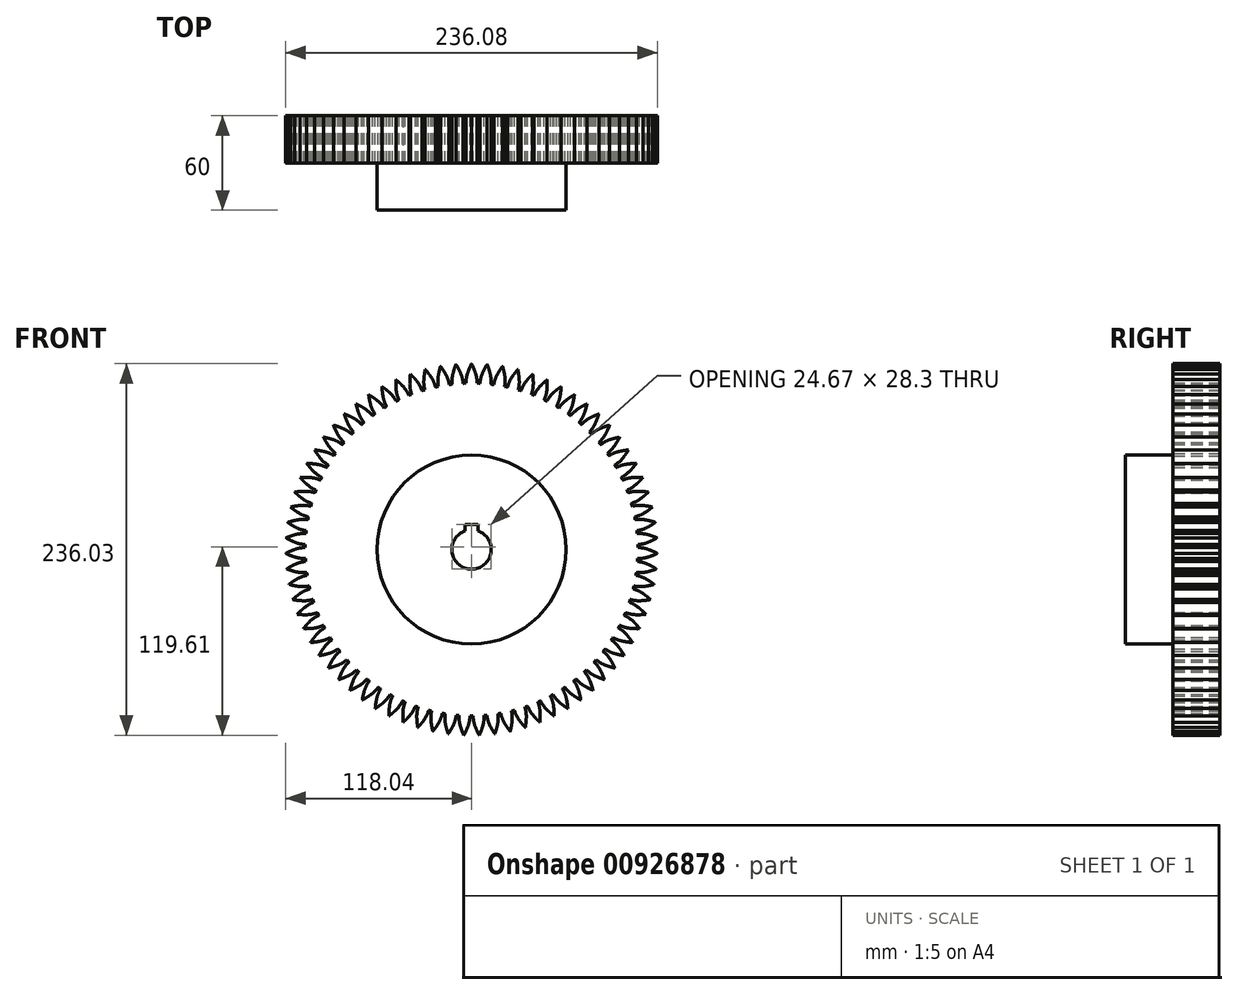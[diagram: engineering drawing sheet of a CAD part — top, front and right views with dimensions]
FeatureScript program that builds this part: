
annotation { "Feature Type Name" : "Feature", "Feature Type Description" : "" }
export const myFeature = defineFeature(function(context is Context, id is Id, definition is map)
    precondition{}
    {
        {
            var Q0;
            Q0=qCreatedBy(makeId("Front.planeOp"),FACE);
            var sketch = newSketch(context, id + "F0", { "sketchPlane" : qUnion([Q0])});
            skCircle(sketch, "E0", {"center": v(0, 0) * mm, "radius": 105.72 * mm});
            skSolve(sketch);
        }
        {
            var Q0;
            Q0=qSketchRegion(id+"F0",true);
            extrude(context, id + "F1", {"entities" : qUnion([Q0]), "depth" : 30 * mm, "offsetDistance" : 25 * mm});
        }
        {
            var Q0;
            Q0=qCreatedBy(makeId("Front.planeOp"),FACE);
            var sketch = newSketch(context, id + "F2", { "sketchPlane" : qUnion([Q0])});
            skCircle(sketch, "E1", {"center": v(0, 0) * mm, "radius": 112.5 * mm, "construction": true});
            skArc(sketch, "E2", {"start": v(50.93, 92.64) * mm, "mid": v(32.1, 100.72) * mm, "end": v(12.06, 105.02) * mm, "construction": true});
            skLineSegment(sketch, "E3", {"start": v(-2.36, 112.48) * mm, "end": v(2.36, 112.48) * mm, "construction": true});
            skLineSegment(sketch, "E4", {"start": v(0, 0) * mm, "end": v(-2.36, 112.48) * mm, "construction": true});
            skLineSegment(sketch, "E5", {"start": v(-2.36, 112.48) * mm, "end": v(34.07, 100.08) * mm, "construction": true});
            skLineSegment(sketch, "E6", {"start": v(0, 0) * mm, "end": v(34.07, 100.08) * mm, "construction": true});
            skLineSegment(sketch, "E7.1.0", {"start": v(0, 0) * mm, "end": v(37.54, 98.83) * mm, "construction": true});
            skLineSegment(sketch, "E7.1.1", {"start": v(1.57, 112.49) * mm, "end": v(37.54, 98.83) * mm, "construction": true});
            skLineSegment(sketch, "E7.2.0", {"start": v(0, 0) * mm, "end": v(40.97, 97.46) * mm, "construction": true});
            skLineSegment(sketch, "E7.2.1", {"start": v(5.5, 112.37) * mm, "end": v(40.97, 97.46) * mm, "construction": true});
            skLineSegment(sketch, "E7.3.0", {"start": v(0, 0) * mm, "end": v(44.34, 95.97) * mm, "construction": true});
            skLineSegment(sketch, "E7.3.1", {"start": v(9.41, 112.1) * mm, "end": v(44.34, 95.97) * mm, "construction": true});
            skLineSegment(sketch, "E7.4.0", {"start": v(0, 0) * mm, "end": v(47.66, 94.36) * mm, "construction": true});
            skLineSegment(sketch, "E7.4.1", {"start": v(13.32, 111.7) * mm, "end": v(47.66, 94.36) * mm, "construction": true});
            skLineSegment(sketch, "E7.5.0", {"start": v(0, 0) * mm, "end": v(50.93, 92.64) * mm, "construction": true});
            skLineSegment(sketch, "E7.5.1", {"start": v(17.21, 111.18) * mm, "end": v(50.93, 92.64) * mm, "construction": true});
            skLineSegment(sketch, "E7.anchor2", {"start": v(0, 0) * mm, "end": v(17.21, 111.18) * mm, "construction": true});
            skLineSegment(sketch, "E8", {"start": v(1.57, 112.49) * mm, "end": v(-1.88, 113.8) * mm, "construction": true});
            skLineSegment(sketch, "E9", {"start": v(5.5, 112.37) * mm, "end": v(-1.3, 115.23) * mm, "construction": true});
            skLineSegment(sketch, "E10", {"start": v(9.41, 112.1) * mm, "end": v(-0.64, 116.75) * mm, "construction": true});
            skLineSegment(sketch, "E11", {"start": v(13.32, 111.7) * mm, "end": v(0.15, 118.36) * mm, "construction": true});
            skLineSegment(sketch, "E12", {"start": v(17.21, 111.18) * mm, "end": v(1.04, 120.06) * mm, "construction": true});
            skFitSpline(sketch, "E13", {"points": [v(-2.36, 112.48) * mm, v(-1.88, 113.8) * mm, v(-1.3, 115.23) * mm, v(-0.64, 116.75) * mm, v(0.15, 118.36) * mm, v(1.04, 120.06) * mm], "startDerivative": vector(7.77, 21.57) * mm, "endDerivative": vector(12.5, 23.7) * mm});
            skArc(sketch, "E14", {"start": v(-2.36, 112.48) * mm, "mid": v(-3.23, 109.12) * mm, "end": v(-3.46, 105.66) * mm});
            skFitSpline(sketch, "E15.MirrorCS", {"points": [v(2.36, 112.48) * mm, v(1.88, 113.8) * mm, v(1.3, 115.23) * mm, v(0.64, 116.75) * mm, v(-0.15, 118.36) * mm, v(-1.04, 120.06) * mm], "startDerivative": vector(-7.77, 21.57) * mm, "endDerivative": vector(-12.5, 23.7) * mm});
            skArc(sketch, "E16.MirrorCS", {"start": v(2.36, 112.48) * mm, "mid": v(3.23, 109.12) * mm, "end": v(3.46, 105.66) * mm});
            skArc(sketch, "E17", {"start": v(1.2, 115.5) * mm, "mid": v(0, 115.5) * mm, "end": v(-1.2, 115.5) * mm});
            skArc(sketch, "E18.trimOffspring", {"start": v(3.46, 105.66) * mm, "mid": v(0, 105.72) * mm, "end": v(-3.46, 105.66) * mm});
            skSolve(sketch);
        }
        {
            var Q0;
            Q0=qSketchRegion(id+"F2",true);
            var Q1;
            Q1=qConstructionFilter(qBodyType(qCreatedBy(id+"F2",EDGE),BodyType.WIRE),ConstructionObject.NO);
            var Q2;
            Q2=makeQuery(id+"F1.opExtrude","CAP_FACE",FACE,{"disambiguationData":[OSD([sQuery(id+"F0.wireOp",EDGE,"E0")])],"isStart":false});
            extrude(context, id + "F3", {"entities" : qUnion([Q0]), "surfaceEntities" : qUnion([Q1]), "endBound" : BoundingType.UP_TO_SURFACE, "depth" : 25 * mm, "endBoundEntityFace" : qUnion([Q2]), "offsetDistance" : 25 * mm});
        }
        {
            var Q0;
            Q0=makeQuery(id+"F3.opExtrude","SWEPT_BODY",BODY,{"disambiguationData":[OSD([sQuery(id+"F2.wireOp",EDGE,"E13"),sQuery(id+"F2.wireOp",EDGE,"E14"),sQuery(id+"F2.wireOp",EDGE,"E15.MirrorCS"),sQuery(id+"F2.wireOp",EDGE,"E16.MirrorCS"),sQuery(id+"F2.wireOp",EDGE,"E17"),sQuery(id+"F2.wireOp",EDGE,"E18.trimOffspring")])]});
            var Q1;
            Q1=makeQuery(id+"F1.opExtrude","SWEPT_FACE",FACE,{"disambiguationData":[OSD([sQuery(id+"F0.wireOp",EDGE,"E0")])]});
            var Q2;
            Q2=makeQuery(id+"F1.opExtrude","SWEPT_BODY",BODY,{"disambiguationData":[OSD([sQuery(id+"F0.wireOp",EDGE,"E0")])]});
            circularPattern(context, id + "F4", {"operationType" : NewBodyOperationType.ADD, "entities" : qUnion([Q0]), "axis" : qUnion([Q1]), "angle" : 360 * degree, "instanceCount" : 75, "equalSpace" : true});
        }
        {
            var Q0;
            {var subQ0=makeQuery(id+"F3.opExtrude","CAP_FACE",FACE,{"disambiguationData":[OSD([sQuery(id+"F2.wireOp",EDGE,"E13"),sQuery(id+"F2.wireOp",EDGE,"E14"),sQuery(id+"F2.wireOp",EDGE,"E15.MirrorCS"),sQuery(id+"F2.wireOp",EDGE,"E16.MirrorCS"),sQuery(id+"F2.wireOp",EDGE,"E17"),sQuery(id+"F2.wireOp",EDGE,"E18.trimOffspring")])],"isStart":false});Q0=makeQuery(id+"F4.boolean.opBoolean","MERGE",FACE,{"derivedFrom":[makeQuery(id+"F1.opExtrude","CAP_FACE",FACE,{"disambiguationData":[OSD([sQuery(id+"F0.wireOp",EDGE,"E0")])],"isStart":false}),subQ0,makeQuery(id+"F4.opPattern","COPY",FACE,{"derivedFrom":subQ0,"instanceName":"1"}),makeQuery(id+"F4.opPattern","COPY",FACE,{"derivedFrom":subQ0,"instanceName":"2"}),makeQuery(id+"F4.opPattern","COPY",FACE,{"derivedFrom":subQ0,"instanceName":"3"}),makeQuery(id+"F4.opPattern","COPY",FACE,{"derivedFrom":subQ0,"instanceName":"4"}),makeQuery(id+"F4.opPattern","COPY",FACE,{"derivedFrom":subQ0,"instanceName":"5"}),makeQuery(id+"F4.opPattern","COPY",FACE,{"derivedFrom":subQ0,"instanceName":"6"}),makeQuery(id+"F4.opPattern","COPY",FACE,{"derivedFrom":subQ0,"instanceName":"7"}),makeQuery(id+"F4.opPattern","COPY",FACE,{"derivedFrom":subQ0,"instanceName":"8"}),makeQuery(id+"F4.opPattern","COPY",FACE,{"derivedFrom":subQ0,"instanceName":"9"}),makeQuery(id+"F4.opPattern","COPY",FACE,{"derivedFrom":subQ0,"instanceName":"10"}),makeQuery(id+"F4.opPattern","COPY",FACE,{"derivedFrom":subQ0,"instanceName":"11"}),makeQuery(id+"F4.opPattern","COPY",FACE,{"derivedFrom":subQ0,"instanceName":"12"}),makeQuery(id+"F4.opPattern","COPY",FACE,{"derivedFrom":subQ0,"instanceName":"13"}),makeQuery(id+"F4.opPattern","COPY",FACE,{"derivedFrom":subQ0,"instanceName":"14"}),makeQuery(id+"F4.opPattern","COPY",FACE,{"derivedFrom":subQ0,"instanceName":"15"}),makeQuery(id+"F4.opPattern","COPY",FACE,{"derivedFrom":subQ0,"instanceName":"16"}),makeQuery(id+"F4.opPattern","COPY",FACE,{"derivedFrom":subQ0,"instanceName":"17"}),makeQuery(id+"F4.opPattern","COPY",FACE,{"derivedFrom":subQ0,"instanceName":"18"}),makeQuery(id+"F4.opPattern","COPY",FACE,{"derivedFrom":subQ0,"instanceName":"19"}),makeQuery(id+"F4.opPattern","COPY",FACE,{"derivedFrom":subQ0,"instanceName":"20"}),makeQuery(id+"F4.opPattern","COPY",FACE,{"derivedFrom":subQ0,"instanceName":"21"}),makeQuery(id+"F4.opPattern","COPY",FACE,{"derivedFrom":subQ0,"instanceName":"22"}),makeQuery(id+"F4.opPattern","COPY",FACE,{"derivedFrom":subQ0,"instanceName":"23"}),makeQuery(id+"F4.opPattern","COPY",FACE,{"derivedFrom":subQ0,"instanceName":"24"}),makeQuery(id+"F4.opPattern","COPY",FACE,{"derivedFrom":subQ0,"instanceName":"25"}),makeQuery(id+"F4.opPattern","COPY",FACE,{"derivedFrom":subQ0,"instanceName":"26"}),makeQuery(id+"F4.opPattern","COPY",FACE,{"derivedFrom":subQ0,"instanceName":"27"}),makeQuery(id+"F4.opPattern","COPY",FACE,{"derivedFrom":subQ0,"instanceName":"28"}),makeQuery(id+"F4.opPattern","COPY",FACE,{"derivedFrom":subQ0,"instanceName":"29"}),makeQuery(id+"F4.opPattern","COPY",FACE,{"derivedFrom":subQ0,"instanceName":"30"}),makeQuery(id+"F4.opPattern","COPY",FACE,{"derivedFrom":subQ0,"instanceName":"31"}),makeQuery(id+"F4.opPattern","COPY",FACE,{"derivedFrom":subQ0,"instanceName":"32"}),makeQuery(id+"F4.opPattern","COPY",FACE,{"derivedFrom":subQ0,"instanceName":"33"}),makeQuery(id+"F4.opPattern","COPY",FACE,{"derivedFrom":subQ0,"instanceName":"34"}),makeQuery(id+"F4.opPattern","COPY",FACE,{"derivedFrom":subQ0,"instanceName":"35"}),makeQuery(id+"F4.opPattern","COPY",FACE,{"derivedFrom":subQ0,"instanceName":"36"}),makeQuery(id+"F4.opPattern","COPY",FACE,{"derivedFrom":subQ0,"instanceName":"37"}),makeQuery(id+"F4.opPattern","COPY",FACE,{"derivedFrom":subQ0,"instanceName":"38"}),makeQuery(id+"F4.opPattern","COPY",FACE,{"derivedFrom":subQ0,"instanceName":"39"}),makeQuery(id+"F4.opPattern","COPY",FACE,{"derivedFrom":subQ0,"instanceName":"40"}),makeQuery(id+"F4.opPattern","COPY",FACE,{"derivedFrom":subQ0,"instanceName":"41"}),makeQuery(id+"F4.opPattern","COPY",FACE,{"derivedFrom":subQ0,"instanceName":"42"}),makeQuery(id+"F4.opPattern","COPY",FACE,{"derivedFrom":subQ0,"instanceName":"43"}),makeQuery(id+"F4.opPattern","COPY",FACE,{"derivedFrom":subQ0,"instanceName":"44"}),makeQuery(id+"F4.opPattern","COPY",FACE,{"derivedFrom":subQ0,"instanceName":"45"}),makeQuery(id+"F4.opPattern","COPY",FACE,{"derivedFrom":subQ0,"instanceName":"46"}),makeQuery(id+"F4.opPattern","COPY",FACE,{"derivedFrom":subQ0,"instanceName":"47"}),makeQuery(id+"F4.opPattern","COPY",FACE,{"derivedFrom":subQ0,"instanceName":"48"}),makeQuery(id+"F4.opPattern","COPY",FACE,{"derivedFrom":subQ0,"instanceName":"49"}),makeQuery(id+"F4.opPattern","COPY",FACE,{"derivedFrom":subQ0,"instanceName":"50"}),makeQuery(id+"F4.opPattern","COPY",FACE,{"derivedFrom":subQ0,"instanceName":"51"}),makeQuery(id+"F4.opPattern","COPY",FACE,{"derivedFrom":subQ0,"instanceName":"52"}),makeQuery(id+"F4.opPattern","COPY",FACE,{"derivedFrom":subQ0,"instanceName":"53"}),makeQuery(id+"F4.opPattern","COPY",FACE,{"derivedFrom":subQ0,"instanceName":"54"}),makeQuery(id+"F4.opPattern","COPY",FACE,{"derivedFrom":subQ0,"instanceName":"55"}),makeQuery(id+"F4.opPattern","COPY",FACE,{"derivedFrom":subQ0,"instanceName":"56"}),makeQuery(id+"F4.opPattern","COPY",FACE,{"derivedFrom":subQ0,"instanceName":"57"}),makeQuery(id+"F4.opPattern","COPY",FACE,{"derivedFrom":subQ0,"instanceName":"58"}),makeQuery(id+"F4.opPattern","COPY",FACE,{"derivedFrom":subQ0,"instanceName":"59"}),makeQuery(id+"F4.opPattern","COPY",FACE,{"derivedFrom":subQ0,"instanceName":"60"}),makeQuery(id+"F4.opPattern","COPY",FACE,{"derivedFrom":subQ0,"instanceName":"61"}),makeQuery(id+"F4.opPattern","COPY",FACE,{"derivedFrom":subQ0,"instanceName":"62"}),makeQuery(id+"F4.opPattern","COPY",FACE,{"derivedFrom":subQ0,"instanceName":"63"}),makeQuery(id+"F4.opPattern","COPY",FACE,{"derivedFrom":subQ0,"instanceName":"64"}),makeQuery(id+"F4.opPattern","COPY",FACE,{"derivedFrom":subQ0,"instanceName":"65"}),makeQuery(id+"F4.opPattern","COPY",FACE,{"derivedFrom":subQ0,"instanceName":"66"}),makeQuery(id+"F4.opPattern","COPY",FACE,{"derivedFrom":subQ0,"instanceName":"67"}),makeQuery(id+"F4.opPattern","COPY",FACE,{"derivedFrom":subQ0,"instanceName":"68"}),makeQuery(id+"F4.opPattern","COPY",FACE,{"derivedFrom":subQ0,"instanceName":"69"}),makeQuery(id+"F4.opPattern","COPY",FACE,{"derivedFrom":subQ0,"instanceName":"70"}),makeQuery(id+"F4.opPattern","COPY",FACE,{"derivedFrom":subQ0,"instanceName":"71"}),makeQuery(id+"F4.opPattern","COPY",FACE,{"derivedFrom":subQ0,"instanceName":"72"}),makeQuery(id+"F4.opPattern","COPY",FACE,{"derivedFrom":subQ0,"instanceName":"73"}),makeQuery(id+"F4.opPattern","COPY",FACE,{"derivedFrom":subQ0,"instanceName":"74"})]});}
            var sketch = newSketch(context, id + "F5", { "sketchPlane" : qUnion([Q0])});
            skCircle(sketch, "E19", {"center": v(0, 0) * mm, "radius": 60 * mm});
            skSolve(sketch);
        }
        {
            var Q0;
            Q0 = qSketchRegion(id + "F5", true);
            extrude(context, id + "F6", {"entities" : qUnion([Q0]), "operationType" : NewBodyOperationType.ADD, "depth" : 30 * mm, "offsetDistance" : 25 * mm});
        }
        {
            var Q0;
            Q0=qCreatedBy(makeId("Front.planeOp"),FACE);
            var sketch = newSketch(context, id + "F7", { "sketchPlane" : qUnion([Q0])});
            skLineSegment(sketch, "E20.top", {"start": v(-4, 15.8) * mm, "end": v(4, 15.8) * mm});
            skLineSegment(sketch, "E20.left", {"start": v(-4, 11.84) * mm, "end": v(-4, 15.8) * mm});
            skLineSegment(sketch, "E20.right", {"start": v(4, 11.84) * mm, "end": v(4, 11.84) * mm});
            skPoint(sketch, "E21.orphan", {"position": v(-4, 0) * mm});
            skLineSegment(sketch, "E22", {"start": v(4, 11.84) * mm, "end": v(4, 15.8) * mm});
            skArc(sketch, "E23", {"start": v(-4, 11.84) * mm, "mid": v(0, -12.5) * mm, "end": v(4, 11.84) * mm});
            skArc(sketch, "E24", {"start": v(4, 11.84) * mm, "mid": v(0, 12.5) * mm, "end": v(-4, 11.84) * mm, "construction": true});
            skSolve(sketch);
        }
        {
            var Q0;
            Q0=qSketchRegion(id+"F7",true);
            extrude(context, id + "F8", {"entities" : qUnion([Q0]), "operationType" : NewBodyOperationType.REMOVE, "endBound" : BoundingType.THROUGH_ALL, "depth" : 25 * mm, "offsetDistance" : 25 * mm});
        }
    });
